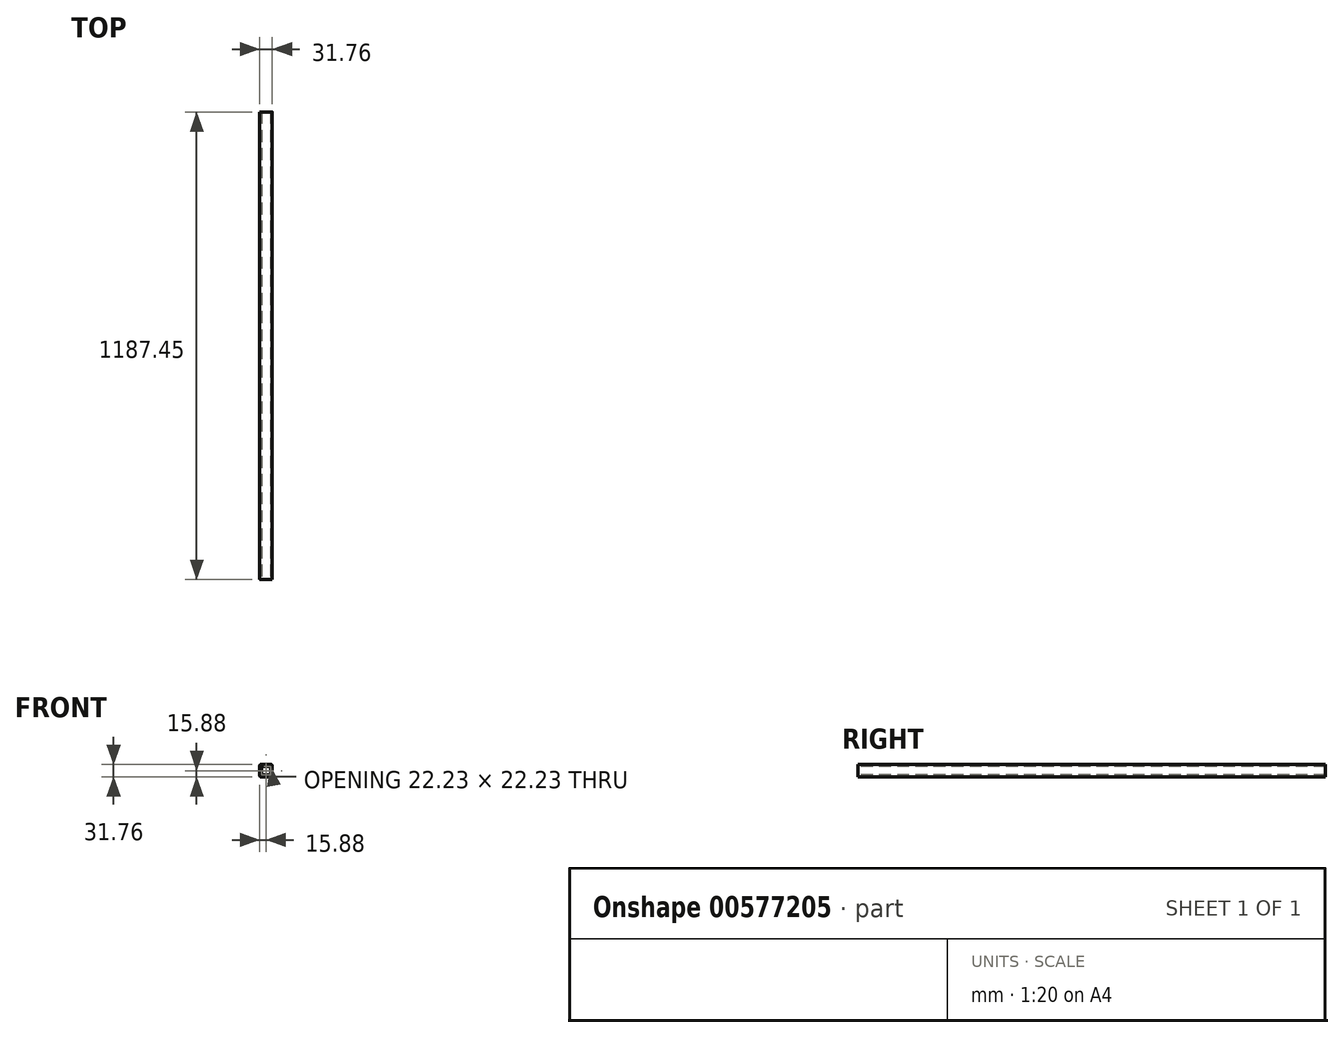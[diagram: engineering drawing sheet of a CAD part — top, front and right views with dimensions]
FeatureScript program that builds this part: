
annotation { "Feature Type Name" : "Feature", "Feature Type Description" : "" }
export const myFeature = defineFeature(function(context is Context, id is Id, definition is map)
    precondition{}
    {
        {
            var Q0;
            Q0=qCreatedBy(makeId("Front.planeOp"),FACE);
            var sketch = newSketch(context, id + "F0", { "sketchPlane" : qUnion([Q0])});
            skLineSegment(sketch, "E0.bottom", {"start": v(7.94, 11.11) * mm, "end": v(-7.94, 11.11) * mm});
            skLineSegment(sketch, "E0.top", {"start": v(7.94, -11.11) * mm, "end": v(-7.94, -11.11) * mm});
            skLineSegment(sketch, "E0.left", {"start": v(11.11, 7.94) * mm, "end": v(11.11, -7.94) * mm});
            skLineSegment(sketch, "E0.right", {"start": v(-11.11, 7.94) * mm, "end": v(-11.11, -7.94) * mm});
            skPoint(sketch, "E0.middle", {"position": v(0, 0) * mm});
            skLineSegment(sketch, "E1.bottom", {"start": v(12.7, 15.88) * mm, "end": v(-12.7, 15.88) * mm});
            skLineSegment(sketch, "E1.top", {"start": v(12.7, -15.88) * mm, "end": v(-12.7, -15.88) * mm});
            skLineSegment(sketch, "E1.left", {"start": v(15.88, 12.7) * mm, "end": v(15.88, -12.7) * mm});
            skLineSegment(sketch, "E1.right", {"start": v(-15.88, 12.7) * mm, "end": v(-15.88, -12.7) * mm});
            skPoint(sketch, "E2.visualSharp", {"position": v(-11.11, 11.11) * mm});
            skArc(sketch, "E2.filletArc", {"start": v(-7.94, 11.11) * mm, "mid": v(-10.18, 10.18) * mm, "end": v(-11.11, 7.94) * mm});
            skPoint(sketch, "E3.visualSharp", {"position": v(-15.88, 15.87) * mm});
            skArc(sketch, "E3.filletArc", {"start": v(-12.7, 15.87) * mm, "mid": v(-14.95, 14.95) * mm, "end": v(-15.88, 12.7) * mm});
            skPoint(sketch, "E4.visualSharp", {"position": v(15.88, 15.88) * mm});
            skArc(sketch, "E4.filletArc", {"start": v(15.88, 12.7) * mm, "mid": v(14.95, 14.95) * mm, "end": v(12.7, 15.88) * mm});
            skPoint(sketch, "E5.visualSharp", {"position": v(11.11, 11.11) * mm});
            skArc(sketch, "E5.filletArc", {"start": v(11.11, 7.94) * mm, "mid": v(10.18, 10.18) * mm, "end": v(7.94, 11.11) * mm});
            skPoint(sketch, "E6.visualSharp", {"position": v(11.11, -11.11) * mm});
            skArc(sketch, "E6.filletArc", {"start": v(7.94, -11.11) * mm, "mid": v(10.18, -10.18) * mm, "end": v(11.11, -7.94) * mm});
            skPoint(sketch, "E7.visualSharp", {"position": v(-11.11, -11.11) * mm});
            skArc(sketch, "E7.filletArc", {"start": v(-11.11, -7.94) * mm, "mid": v(-10.18, -10.18) * mm, "end": v(-7.94, -11.11) * mm});
            skPoint(sketch, "E8.visualSharp", {"position": v(15.88, -15.88) * mm});
            skArc(sketch, "E8.filletArc", {"start": v(12.7, -15.87) * mm, "mid": v(14.95, -14.95) * mm, "end": v(15.88, -12.7) * mm});
            skPoint(sketch, "E9.visualSharp", {"position": v(-15.88, -15.88) * mm});
            skArc(sketch, "E9.filletArc", {"start": v(-15.88, -12.7) * mm, "mid": v(-14.95, -14.95) * mm, "end": v(-12.7, -15.88) * mm});
            skSolve(sketch);
        }
        {
            var Q0;
            Q0 = qSketchRegion(id + "F0", true);
            extrude(context, id + "F1", {"entities" : qUnion([Q0]), "oppositeDirection" : true, "depth" : 1187.45 * mm, "offsetDistance" : 25.4 * mm});
        }
    });
